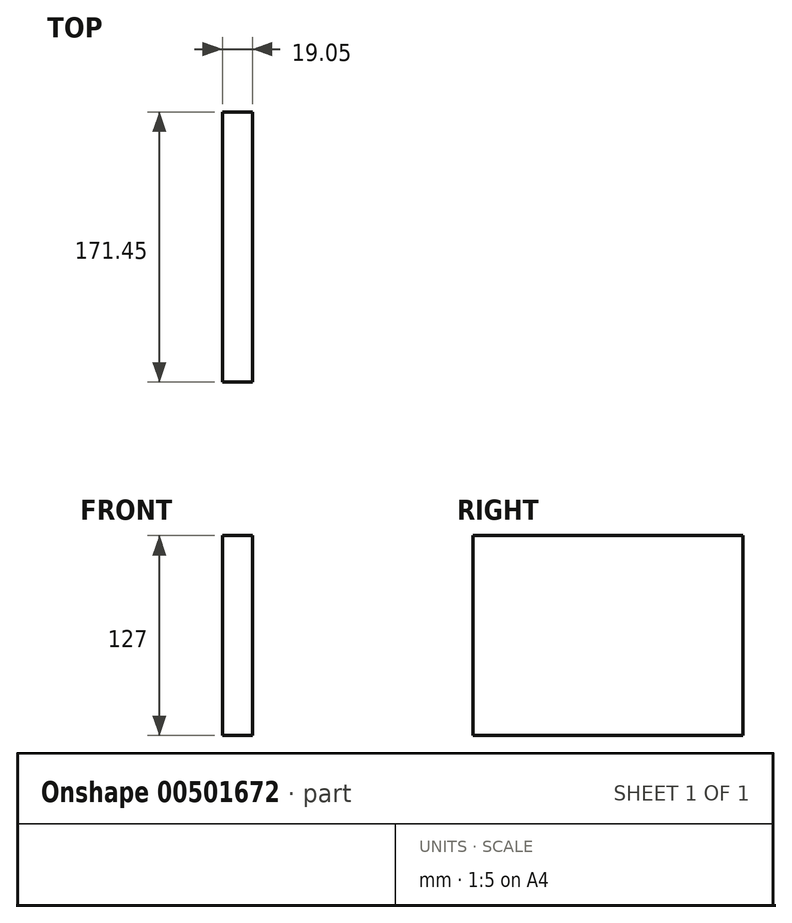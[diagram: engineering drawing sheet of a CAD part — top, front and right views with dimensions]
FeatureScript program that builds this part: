
annotation { "Feature Type Name" : "Feature", "Feature Type Description" : "" }
export const myFeature = defineFeature(function(context is Context, id is Id, definition is map)
    precondition{}
    {
        {
            var Q0;
            Q0=qCreatedBy(makeId("Right.planeOp"),FACE);
            var sketch = newSketch(context, id + "F0", { "sketchPlane" : qUnion([Q0])});
            skLineSegment(sketch, "E0.bottom", {"start": v(0, 0) * mm, "end": v(171.45, 0) * mm});
            skLineSegment(sketch, "E0.top", {"start": v(0, 127) * mm, "end": v(171.45, 127) * mm});
            skLineSegment(sketch, "E0.left", {"start": v(0, 0) * mm, "end": v(0, 127) * mm});
            skLineSegment(sketch, "E0.right", {"start": v(171.45, 0) * mm, "end": v(171.45, 127) * mm});
            skSolve(sketch);
        }
        {
            var Q0;
            Q0 = qSketchRegion(id + "F0", true);
            extrude(context, id + "F1", {"entities" : qUnion([Q0]), "depth" : 19.05 * mm});
        }
    });
